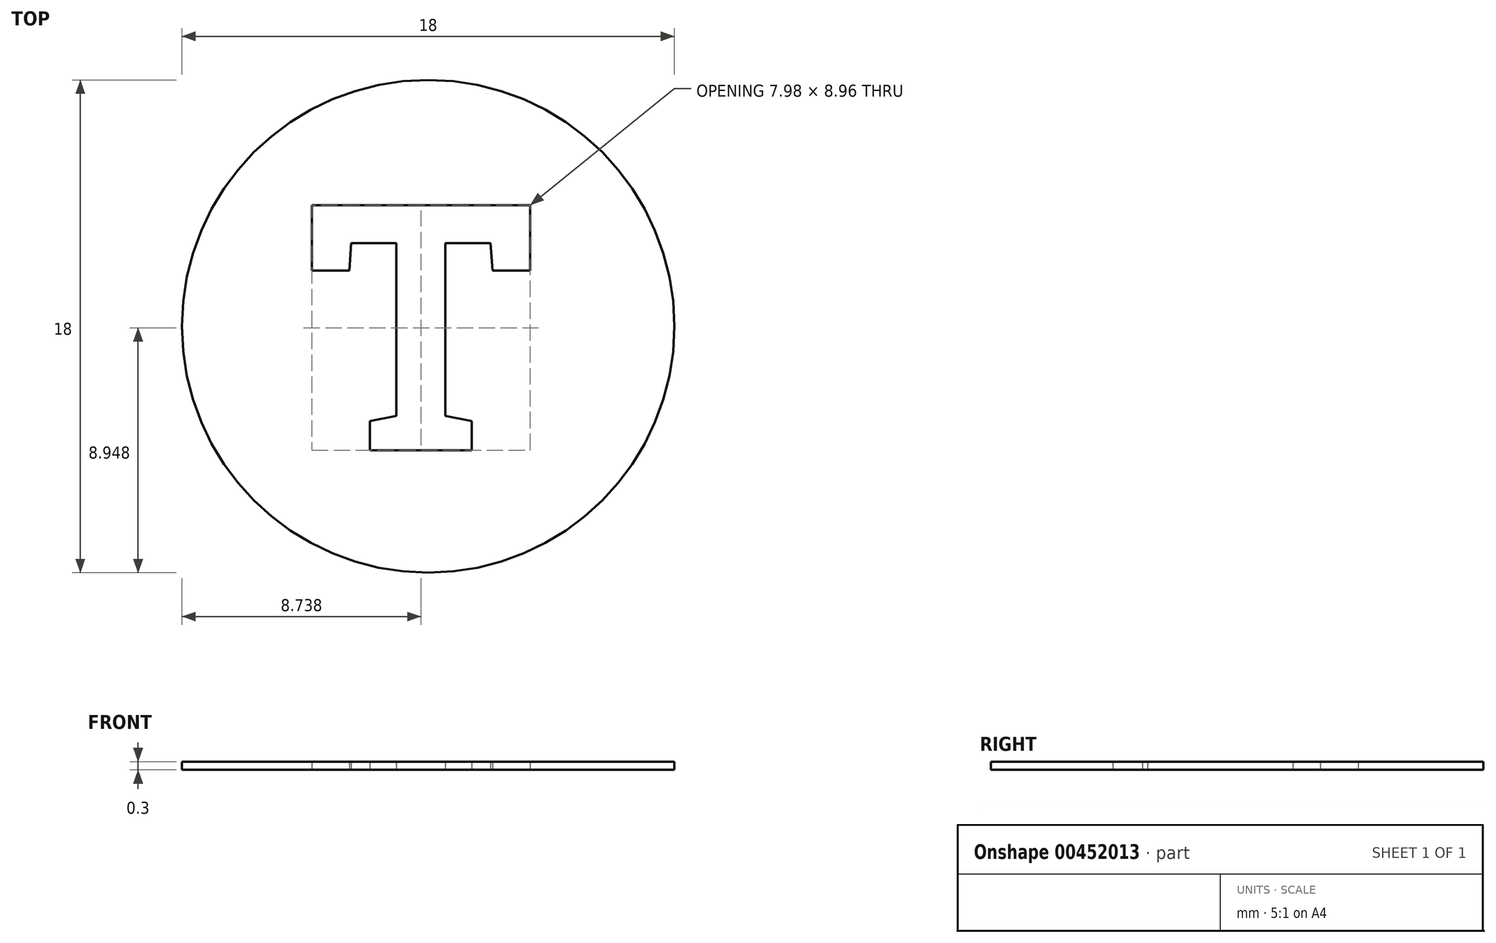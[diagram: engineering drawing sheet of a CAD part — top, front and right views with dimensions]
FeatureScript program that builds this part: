
annotation { "Feature Type Name" : "Feature", "Feature Type Description" : "" }
export const myFeature = defineFeature(function(context is Context, id is Id, definition is map)
    precondition{}
    {
        {
            var Q0;
            Q0=qCreatedBy(makeId("Top.planeOp"),FACE);
            var sketch = newSketch(context, id + "F0", { "sketchPlane" : qUnion([Q0])});
            skCircle(sketch, "E0", {"center": v(-38.31, 25.11) * mm, "radius": 9 * mm});
            skText(sketch, "E1", { "text": "T", "fontName": "RobotoSlab-Bold.ttf"});
            skLineSegment(sketch, "E2", {"start": v(-38.31, 29.65) * mm, "end": v(-38.31, 34.11) * mm, "construction": true});
            skLineSegment(sketch, "E3", {"start": v(-38.31, 20.58) * mm, "end": v(-38.31, 16.11) * mm, "construction": true});
            const initialGuessF0  = {"E1": [-0.04281, 0.02058, 1, 0, 0.00907]};
            skSetInitialGuess(sketch, initialGuessF0);
            skSolve(sketch);
        }
        {
            var Q0;
            Q0=makeQuery(id+"F0.imprint","IMPRINT",FACE,{"disambiguationData":[TD([[makeQuery(id+"F0.imprint","IMPRINT",EDGE,{"derivedFrom":sQuery(id+"F0.wireOp",EDGE,"E0")}),1.0]])]});
            extrude(context, id + "F1", {"entities" : qUnion([Q0]), "depth" : .3 * mm});
        }
    });
